# Revit family: ACV Angle Series
name_source: partatom
category: Generic Models
revit_build: Autodesk Revit 2014 (Build: 20130308_1515(x64)
units: mm (PartAtom-declared; Revit-internal decimal feet)

## types (6) — shared parameters
5WIDTH = 1.73 "
AB = 13.25 "
BODY = Iron, Cast
Description = BEECO ACV Angle Series
EXTRUDE H = 1.86 "
HOLE1 = 3.47 "
MATERIAL = Iron, Cast
Manufacturer = MIFAB
ON/OFF = No
URL = www.mifab.com

## per-type parameters (varying)
- ACV1.50: 2H=2.5 "; 2OD=0.9 "; 2RP=2 "; 3AW=3.35 "; 3FILLET=0.5 "; 3ID=1.84 "; 3LENGTH=7 "; 5EXT=3.22 "; 5EXT1=3.4 "; 5HOLE=0.1 "; 5RP=3.1 "; 5WID=0.8 "; 6H=3.05 "; 6RADI=0.1 "; 7L=2.75 "; 7RA=1.75 "; 8H=2.25 "; 8L=2.5 "; 8R1=0.5 "; 8R2=2.25 "; 9HH=1.25 "; 9RA=2 "; 9THK=0.35 "; AH=12 "; AL=8.18 "; AR=4.18 "; AW=6.69 "; Dia.=2 "; EXTRUDE L=0.75 "; EXTRUDE W=0.65 "; End extru=2.5 "; FLANGE1=0.56 "; FLANGE1-1=0.65 "; FLANGE1-2=0.04 "; FLANGE2=0.64 "; HOLE=0.3 "; HOLE RP=2.5 "; Hole1=0.3 "; Hole2=0.6 "; IN=1.8 "; INNER OUT1=2.8 "; OUT=1.9 "; RADI=1.21 "; RADI1-2=1 "; UPPER H1=1.6 "; UPPER OUT1=1.5 "; Up 1=0.7 "; Up 2=0.4 "; rp4=2 "; up 3=0.21 "
- ACV2.00: 2H=3.8 "; 2OD=1.2 "; 2RP=3 "; 3AW=3.94 "; 3FILLET=0.45 "; 3ID=2.52 "; 3LENGTH=9 "; 5EXT=3.35 "; 5EXT1=3.6 "; 5HOLE=0.18 "; 5RP=3.35 "; 5WID=1.16 "; 6H=3.4 "; 6RADI=0.15 "; 7L=2.75 "; 7RA=2.25 "; 8H=2.5 "; 8L=3.25 "; 8R1=0.75 "; 8R2=2.5 "; 9HH=2 "; 9RA=2 "; 9THK=0.5 "; AH=16.31 "; AL=9.81 "; AR=5.44 "; AW=7.88 "; Dia.=3 "; EXTRUDE L=0.8 "; EXTRUDE W=1 "; End extru=3 "; FLANGE1=0.63 "; FLANGE1-1=0.8 "; FLANGE1-2=0.06 "; FLANGE2=0.71 "; HOLE=0.4 "; HOLE RP=2.8 "; Hole1=0.45 "; Hole2=0.75 "; IN=1.8 "; INNER OUT1=2.8 "; OUT=2.5 "; RADI=1.5 "; RADI1-2=1.1 "; UPPER H1=2.8 "; UPPER OUT1=1.8 "; Up 1=0.89 "; Up 2=0.54 "; rp4=2.2 "; up 3=0.4 "
- ACV2.50: 2H=3.8 "; 2OD=1.4 "; 2RP=3.5 "; 3AW=4.63 "; 3FILLET=0.5 "; 3ID=3 "; 3LENGTH=10 "; 5EXT=3.26 "; 5EXT1=3.6 "; 5HOLE=0.18 "; 5RP=3.35 "; 5WID=1.3 "; 6H=3.95 "; 6RADI=0.2 "; 7L=2.75 "; 7RA=2.75 "; 8H=2.75 "; 8L=3.76 "; 8R1=0.75 "; 8R2=2 "; 9HH=1.85 "; 9RA=2.75 "; 9THK=0.65 "; AH=17.5 "; AL=11.06 "; AR=5.81 "; AW=9.25 "; Dia.=4 "; EXTRUDE L=1 "; EXTRUDE W=1 "; End extru=3.5 "; FLANGE1=0.6 "; FLANGE1-1=0.8 "; FLANGE1-2=0.06 "; FLANGE2=0.68 "; HOLE=0.45 "; HOLE RP=3.5 "; Hole1=0.55 "; Hole2=0.85 "; IN=2.2 "; INNER OUT1=3.3 "; OUT=3.2 "; RADI=2 "; RADI1-2=1.8 "; UPPER H1=3 "; UPPER OUT1=2 "; Up 1=1 "; Up 2=0.6 "; rp4=2.4 "; up 3=0.5 "
- ACV3.00: 2H=4.2 "; 2OD=1.2 "; 2RP=4.5 "; 3AW=6.5 "; 3FILLET=0.75 "; 3ID=4 "; 3LENGTH=14 "; 5EXT=5.14 "; 5EXT1=5.8 "; 5HOLE=0.18 "; 5RP=3.35 "; 5WID=1.7 "; 6H=5.75 "; 6RADI=0.25 "; 7L=3.75 "; 7RA=3.75 "; 8H=3.5 "; 8L=5.5 "; 8R1=1 "; 8R2=3 "; 9HH=2 "; 9RA=3.55 "; 9THK=0.7 "; AH=22.44 "; AL=16 "; AR=7.06 "; AW=13 "; Dia.=6 "; EXTRUDE L=1.4 "; EXTRUDE W=1.25 "; End extru=4.75 "; FLANGE1=0.8 "; FLANGE1-1=1.1 "; FLANGE1-2=0.06 "; FLANGE2=0.88 "; HOLE=0.55 "; HOLE RP=5 "; Hole1=0.56 "; Hole2=0.86 "; IN=1.99 "; INNER OUT1=5 "; OUT=4 "; RADI=3 "; RADI1-2=2.8 "; UPPER H1=3.5 "; UPPER OUT1=3.2 "; Up 1=1.7 "; Up 2=1.2 "; rp4=2.6 "; up 3=0.6 "
- ACV4.00: 2H=5 "; 2OD=1.5 "; 2RP=5 "; 3AW=8.16 "; 3FILLET=0.5 "; 3ID=5 "; 3LENGTH=17 "; 5EXT=6.31 "; 5EXT1=7 "; 5HOLE=0.18 "; 5RP=3.35 "; 5WID=2 "; 6H=7.25 "; 6RADI=0.3 "; 7L=2.75 "; 7RA=4.5 "; 8H=4 "; 8L=6.5 "; 8R1=1.25 "; 8R2=2 "; 9HH=5 "; 9RA=3.95 "; 9THK=0.75 "; AH=25 "; AL=18.88 "; AR=11.81 "; AW=16.31 "; Dia.=8 "; EXTRUDE L=2.5 "; EXTRUDE W=2 "; End extru=6 "; FLANGE1=1 "; FLANGE1-1=1.2 "; FLANGE1-2=0.08 "; FLANGE2=1.08 "; HOLE=0.7 "; HOLE RP=6.25 "; Hole1=0.8 "; Hole2=1.1 "; IN=3.5 "; INNER OUT1=6.5 "; OUT=5 "; RADI=3.75 "; RADI1-2=3 "; UPPER H1=4 "; UPPER OUT1=3 "; Up 1=1.6 "; Up 2=1.2 "; rp4=4.25 "; up 3=0.7 "
- ACV6.00: 2H=7 "; 2OD=2.2 "; 2RP=5 "; 3AW=9.75 "; 3FILLET=1 "; 3ID=6 "; 3LENGTH=19 "; 5EXT=8.15 "; 5EXT1=8.5 "; 5HOLE=0.18 "; 5RP=3.35 "; 5WID=2.5 "; 6H=8.85 "; 6RADI=0.35 "; 7L=2.75 "; 7RA=5.5 "; 8H=6 "; 8L=8 "; 8R1=2 "; 8R2=5 "; 9HH=5 "; 9RA=6 "; 9THK=0.95 "; AH=32.25 "; AL=23 "; AR=13.31 "; AW=19.5 "; Dia.=10 "; EXTRUDE L=3 "; EXTRUDE W=2 "; End extru=7 "; FLANGE1=1.25 "; FLANGE1-1=1.25 "; FLANGE1-2=0.1 "; FLANGE2=1.33 "; HOLE=0.85 "; HOLE RP=7.66 "; Hole1=1 "; Hole2=1.3 "; IN=4.95 "; INNER OUT1=8 "; OUT=6 "; RADI=4 "; RADI1-2=3.2 "; UPPER H1=6 "; UPPER OUT1=3.75 "; Up 1=2 "; Up 2=1.5 "; rp4=5 "; up 3=0.8 "

note: column(s) folded — value = type name in every type: Model

## geometry (parser evidence)
native form markers: Sweep x1
no freeform markers — native parametric forms only
